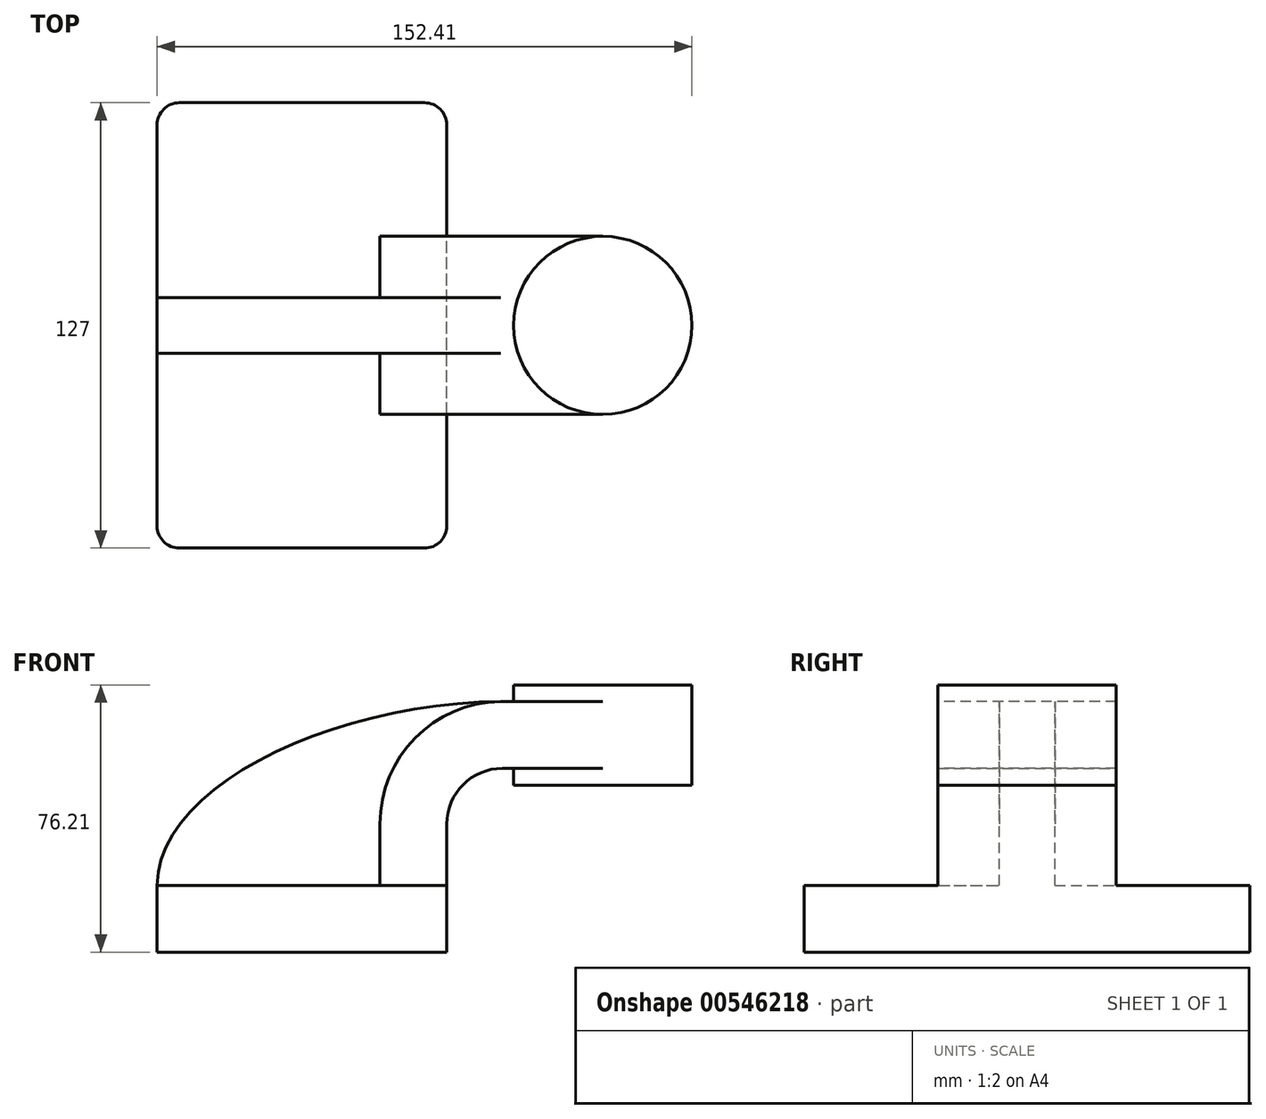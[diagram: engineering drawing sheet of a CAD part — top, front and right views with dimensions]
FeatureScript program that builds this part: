
annotation { "Feature Type Name" : "Feature", "Feature Type Description" : "" }
export const myFeature = defineFeature(function(context is Context, id is Id, definition is map)
    precondition{}
    {
        {
            var Q0;
            Q0=qCreatedBy(makeId("Front.planeOp"),FACE);
            var sketch = newSketch(context, id + "F0", { "sketchPlane" : qUnion([Q0])});
            skLineSegment(sketch, "E0.bottom", {"start": v(41.27, 9.53) * mm, "end": v(-41.28, 9.53) * mm});
            skLineSegment(sketch, "E0.top", {"start": v(41.28, -9.52) * mm, "end": v(-41.27, -9.52) * mm});
            skLineSegment(sketch, "E0.left", {"start": v(41.28, 9.53) * mm, "end": v(41.28, -9.52) * mm});
            skLineSegment(sketch, "E0.right", {"start": v(-41.28, 9.53) * mm, "end": v(-41.27, -9.52) * mm});
            skPoint(sketch, "E0.middle", {"position": v(0, 0) * mm});
            skLineSegment(sketch, "E1.bottom", {"start": v(60.32, 38.1) * mm, "end": v(111.12, 38.1) * mm});
            skLineSegment(sketch, "E1.top", {"start": v(60.32, 66.68) * mm, "end": v(111.12, 66.68) * mm});
            skLineSegment(sketch, "E1.left", {"start": v(60.32, 38.1) * mm, "end": v(60.32, 66.68) * mm});
            skLineSegment(sketch, "E1.right", {"start": v(111.13, 38.1) * mm, "end": v(111.12, 66.68) * mm});
            skPoint(sketch, "E1.middle", {"position": v(85.72, 52.39) * mm});
            skLineSegment(sketch, "E2", {"start": v(41.27, 9.53) * mm, "end": v(41.27, 27) * mm});
            skArc(sketch, "E3", {"start": v(41.27, 27) * mm, "mid": v(45.92, 38.23) * mm, "end": v(57.15, 42.88) * mm});
            skLineSegment(sketch, "E4", {"start": v(57.15, 42.88) * mm, "end": v(85.72, 42.88) * mm});
            skLineSegment(sketch, "E5.0", {"start": v(57.15, 61.93) * mm, "end": v(85.72, 61.93) * mm});
            skArc(sketch, "E5.1", {"start": v(22.22, 27) * mm, "mid": v(32.45, 51.7) * mm, "end": v(57.15, 61.93) * mm});
            skLineSegment(sketch, "E5.2", {"start": v(22.22, 9.53) * mm, "end": v(22.22, 27) * mm});
            skFitSpline(sketch, "E6", {"points": [v(-41.28, 9.53) * mm, v(57.15, 61.93) * mm], "startDerivative": vector(0.4, 86.34) * mm, "endDerivative": vector(141.82, 0.79) * mm});
            skLineSegment(sketch, "E7", {"start": v(85.72, 66.68) * mm, "end": v(85.72, 38.1) * mm});
            skSolve(sketch);
        }
        {
            var Q0;
            Q0=makeQuery(id+"F0.imprint","IMPRINT",FACE,{"disambiguationData":[TD([[makeQuery(id+"F0.imprint","IMPRINT",EDGE,{"derivedFrom":sQuery(id+"F0.wireOp",EDGE,"E0.top")}),-1.0]])]});
            extrude(context, id + "F1", {"entities" : qUnion([Q0]), "endBound" : BoundingType.SYMMETRIC, "depth" : 127 * mm, "offsetDistance" : 25.4 * mm});
        }
        {
            var Q0;
            {var subQ1=sQuery(id+"F0.wireOp",EDGE,"E2");Q0=makeQuery(id+"F0.imprint","IMPRINT",FACE,{"disambiguationData":[TD([[makeQuery(id+"F0.imprint","IMPRINT",EDGE,{"derivedFrom":subQ1}),1.0]])]});}
            var Q1;
            {var subQ0=sQuery(id+"F0.wireOp",EDGE,"E4");var subQ1=sQuery(id+"F0.wireOp",EDGE,"E1.left");var subQ2=makeQuery(id+"F0.imprint","INTERSECT",VERTEX,{"derivedFrom":[subQ1,subQ0]});Q1=makeQuery(id+"F0.imprint","IMPRINT",FACE,{"disambiguationData":[TD([[makeQuery(id+"F0.imprint","IMPRINT",EDGE,{"disambiguationData":[TD([[subQ2,-1.0]])],"derivedFrom":subQ1}),-1.0]])]});}
            extrude(context, id + "F2", {"entities" : qUnion([Q0, Q1]), "operationType" : NewBodyOperationType.ADD, "endBound" : BoundingType.SYMMETRIC, "depth" : 50.8 * mm, "offsetDistance" : 25.4 * mm});
        }
        {
            var Q0;
            {var subQ3=sQuery(id+"F0.wireOp",EDGE,"E5.2");Q0=makeQuery(id+"F0.imprint","IMPRINT",FACE,{"disambiguationData":[TD([[makeQuery(id+"F0.imprint","IMPRINT",EDGE,{"derivedFrom":subQ3}),1.0]])]});}
            extrude(context, id + "F3", {"entities" : qUnion([Q0]), "operationType" : NewBodyOperationType.ADD, "endBound" : BoundingType.SYMMETRIC, "depth" : 15.88 * mm, "offsetDistance" : 25.4 * mm});
        }
        {
            var Q0;
            {var subQ4=sQuery(id+"F0.wireOp",EDGE,"E1.right");Q0=makeQuery(id+"F0.imprint","IMPRINT",FACE,{"disambiguationData":[TD([[makeQuery(id+"F0.imprint","IMPRINT",EDGE,{"derivedFrom":subQ4}),1.0]])]});}
            var Q1;
            Q1=sQuery(id+"F0.wireOp",EDGE,"E7");
            revolve(context, id + "F4", {"operationType" : NewBodyOperationType.ADD, "entities" : qUnion([Q0]), "axis" : qUnion([Q1]), "revolveType" : RevolveType.FULL});
        }
        {
            var Q0;
            Q0=makeQuery(id+"F1.opExtrude","CAP_EDGE",EDGE,{"disambiguationData":[OSD([sQuery(id+"F0.wireOp",EDGE,"E0.left")])],"isStart":false});
            var Q1;
            Q1=makeQuery(id+"F1.opExtrude","CAP_EDGE",EDGE,{"disambiguationData":[OSD([sQuery(id+"F0.wireOp",EDGE,"E0.right")])],"isStart":false});
            var Q2;
            Q2=makeQuery(id+"F1.opExtrude","CAP_EDGE",EDGE,{"disambiguationData":[OSD([sQuery(id+"F0.wireOp",EDGE,"E0.left")])],"isStart":true});
            var Q3;
            Q3=makeQuery(id+"F1.opExtrude","CAP_EDGE",EDGE,{"disambiguationData":[OSD([sQuery(id+"F0.wireOp",EDGE,"E0.right")])],"isStart":true});
            fillet(context, id + "F5", {"entities" : qUnion([Q0, Q1, Q2, Q3]), "radius" : 6.35 * mm, "tangentPropagation" : true, "allowEdgeOverflow" : false});
        }
    });
